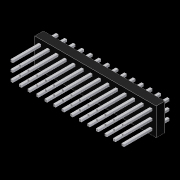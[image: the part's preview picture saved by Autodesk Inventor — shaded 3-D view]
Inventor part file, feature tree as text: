
AUTODESK INVENTOR PART (.ipt)
format: ipt  version: 2012 (Build 160160000, 160)  size: 323,072 bytes
history: native  units: in
note: dims shown in document units (in); Inventor stores cm internally (conversion verified against a paired STEP export)
features: extrude x3, sketch x1, pattern_linear x1
ambient origin geometry x8: Origin, YZ Plane, XZ Plane, XY Plane, X Axis, Y Axis, Z Axis, Center Point
bodies: Solid1 (feature_tree)
feature tree (5):
  sketch  "Sketch1"  dims[d0=0.0in d1=0.025in d2=0.025in d3=0.025in d4=0.025in d6=0.0475in d7=0.0475in d8=0.1in d9=0.0in d10=0.33in d11=0.0in d12=5.5118in d14=0.1in d15=1.1811in d17=0.1in d18=0.2in d19=0.0in]
  extrude  "Extrusion1"  Depth=0.025in
  extrude  "Extrusion2"  Depth=0.025in
  extrude  "Extrusion3"  Depth=0.025in
  pattern_linear  "Rectangular Pattern1"  Spacing1=0.025in  [1 undecoded]
note: 1 required parameter value undecoded (feature->parameter linkage not recoverable at this tier; creation-order binding heuristic only, values carry confidence <= 0.55)
